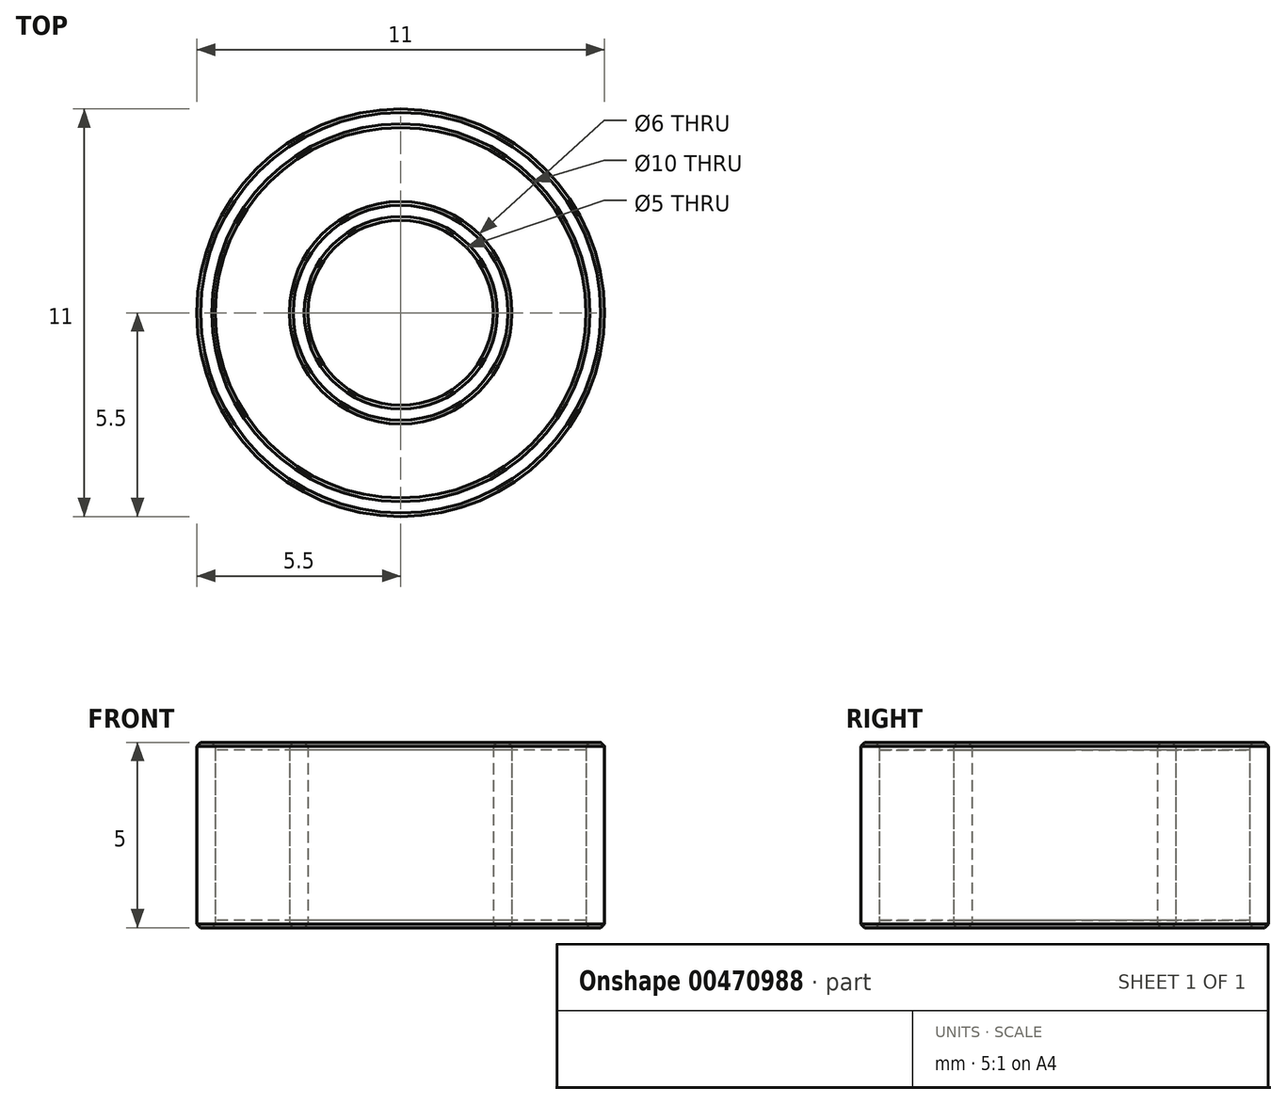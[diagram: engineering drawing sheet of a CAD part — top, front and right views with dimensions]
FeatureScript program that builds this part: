
annotation { "Feature Type Name" : "Feature", "Feature Type Description" : "" }
export const myFeature = defineFeature(function(context is Context, id is Id, definition is map)
    precondition{}
    {
        {
            var Q0;
            Q0=qCreatedBy(makeId("Top.planeOp"),FACE);
            var sketch = newSketch(context, id + "F0", { "sketchPlane" : qUnion([Q0])});
            skCircle(sketch, "E0", {"center": v(0, 0) * mm, "radius": 5.5 * mm});
            skCircle(sketch, "E1", {"center": v(0, 0) * mm, "radius": 2.5 * mm});
            skCircle(sketch, "E2.0", {"center": v(0, 0) * mm, "radius": 5 * mm});
            skCircle(sketch, "E3.0", {"center": v(0, 0) * mm, "radius": 3 * mm});
            skSolve(sketch);
        }
        {
            var Q0;
            Q0=makeQuery(id+"F0.imprint","IMPRINT",FACE,{"disambiguationData":[TD([[makeQuery(id+"F0.imprint","IMPRINT",EDGE,{"derivedFrom":sQuery(id+"F0.wireOp",EDGE,"E1")}),-1.0]])]});
            var Q1;
            Q1=makeQuery(id+"F0.imprint","IMPRINT",FACE,{"disambiguationData":[TD([[makeQuery(id+"F0.imprint","IMPRINT",EDGE,{"derivedFrom":sQuery(id+"F0.wireOp",EDGE,"E0")}),1.0]])]});
            extrude(context, id + "F1", {"entities" : qUnion([Q0, Q1]), "depth" : 5 * mm});
        }
        {
            var Q0;
            Q0=makeQuery(id+"F0.imprint","IMPRINT",FACE,{"disambiguationData":[TD([[makeQuery(id+"F0.imprint","IMPRINT",EDGE,{"derivedFrom":sQuery(id+"F0.wireOp",EDGE,"E2.0")}),1.0]])]});
            extrude(context, id + "F2", {"entities" : qUnion([Q0]), "depth" : 4.8 * mm, "hasSecondDirection" : true, "secondDirectionOppositeDirection" : false, "secondDirectionDepth" : 0.2 * mm});
        }
        {
            var Q0;
            {var subQ0=sQuery(id+"F0.wireOp",EDGE,"E0");Q0=makeQuery(id+"F0BHlAFDJWVW7Y7_1.boolean.opBoolean","MERGE",FACE,{"derivedFrom":[makeQuery(id+"F1.opExtrude","CAP_FACE",FACE,{"disambiguationData":[OSD([subQ0,sQuery(id+"F0.wireOp",EDGE,"E2.0")])],"isStart":true}),makeQuery(id+"F0BHlAFDJWVW7Y7_1.opExtrude","CAP_FACE",FACE,{"disambiguationData":[OSD([sQuery(id+"F0.wireOp",EDGE,"MePryiGi-OmUY-C7yO-MmJH-qqiRuWpCLKw8"),subQ0])],"isStart":true})]});}
            var Q1;
            Q1=makeQuery(id+"F1.opExtrude","CAP_FACE",FACE,{"disambiguationData":[OSD([sQuery(id+"F0.wireOp",EDGE,"E1"),sQuery(id+"F0.wireOp",EDGE,"E3.0")])],"isStart":true});
            var Q2;
            Q2=makeQuery(id+"F1.opExtrude","CAP_FACE",FACE,{"disambiguationData":[OSD([sQuery(id+"F0.wireOp",EDGE,"E0"),sQuery(id+"F0.wireOp",EDGE,"E2.0")])],"isStart":false});
            var Q3;
            Q3=makeQuery(id+"F1.opExtrude","CAP_FACE",FACE,{"disambiguationData":[OSD([sQuery(id+"F0.wireOp",EDGE,"E1"),sQuery(id+"F0.wireOp",EDGE,"E3.0")])],"isStart":false});
            var Q4;
            Q4=makeQuery(id+"F0BHlAFDJWVW7Y7_1.opExtrude","CAP_EDGE",EDGE,{"disambiguationData":[OSD([sQuery(id+"F0.wireOp",EDGE,"MePryiGi-OmUY-C7yO-MmJH-qqiRuWpCLKw8")])],"isStart":false});
            chamfer(context, id + "F3", {"entities" : qUnion([Q0, Q1, Q2, Q3, Q4]), "width" : 0.1 * mm, "tangentPropagation" : true});
        }
    });
